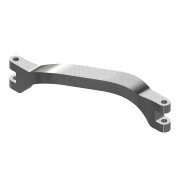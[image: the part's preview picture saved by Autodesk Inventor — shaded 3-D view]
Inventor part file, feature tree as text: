
AUTODESK INVENTOR PART (.ipt)
format: ipt  version: 2020 (Build 240168000, 168)  size: 480,256 bytes
history: native  units: mm
features: extrude x4, sketch x4, other x2, fillet x1, projected_geometry x1
ambient origin geometry x8: Origin, YZ Plane, XZ Plane, XY Plane, X Axis, Y Axis, Z Axis, Center Point
bodies: Solid1 (feature_tree)
feature tree (12):
  extrude  "Extrusion1"  Depth=13.75mm
  extrude  "Extrusion2"  Depth=2.75mm
  extrude  "Extrusion3"  Depth=1.375mm
  fillet  "Fillet1"  Radius=2.0625mm
  extrude  "Extrusion4"  TaperAngle=30.0deg  [1 undecoded]
  sketch  "Sketch1"  dims[d0=35.75mm d1=13.75mm]
  sketch  "Sketch2"  dims[d2=8.937mm d3=0.0mm d27=2.75mm]
  other  "Image1"
  projected_geometry  "Projected Loop1"
  sketch  "Sketch3"  dims[d28=1.375mm d29=3.3386mm d30=2.0625mm]
  other  "Image2"
  sketch  "Sketch4"  dims[d31=120.0deg d33=30.0deg d46=1.3749mm d47=1.3749mm d48=8.937mm d49=0.0mm d67=2.035mm d68=2.777mm d69=2.8mm d70=2.035mm d71=2.75mm d73=0.25mm d76=0.0mm d77=0.0mm d78=2.0mm d79=4.8125mm d80=150.0deg d81=1.375mm d82=0.75mm d83=0.7327mm d84=0.0mm d85=0.0mm]
note: 1 required parameter value undecoded (feature->parameter linkage not recoverable at this tier; creation-order binding heuristic only, values carry confidence <= 0.55)
